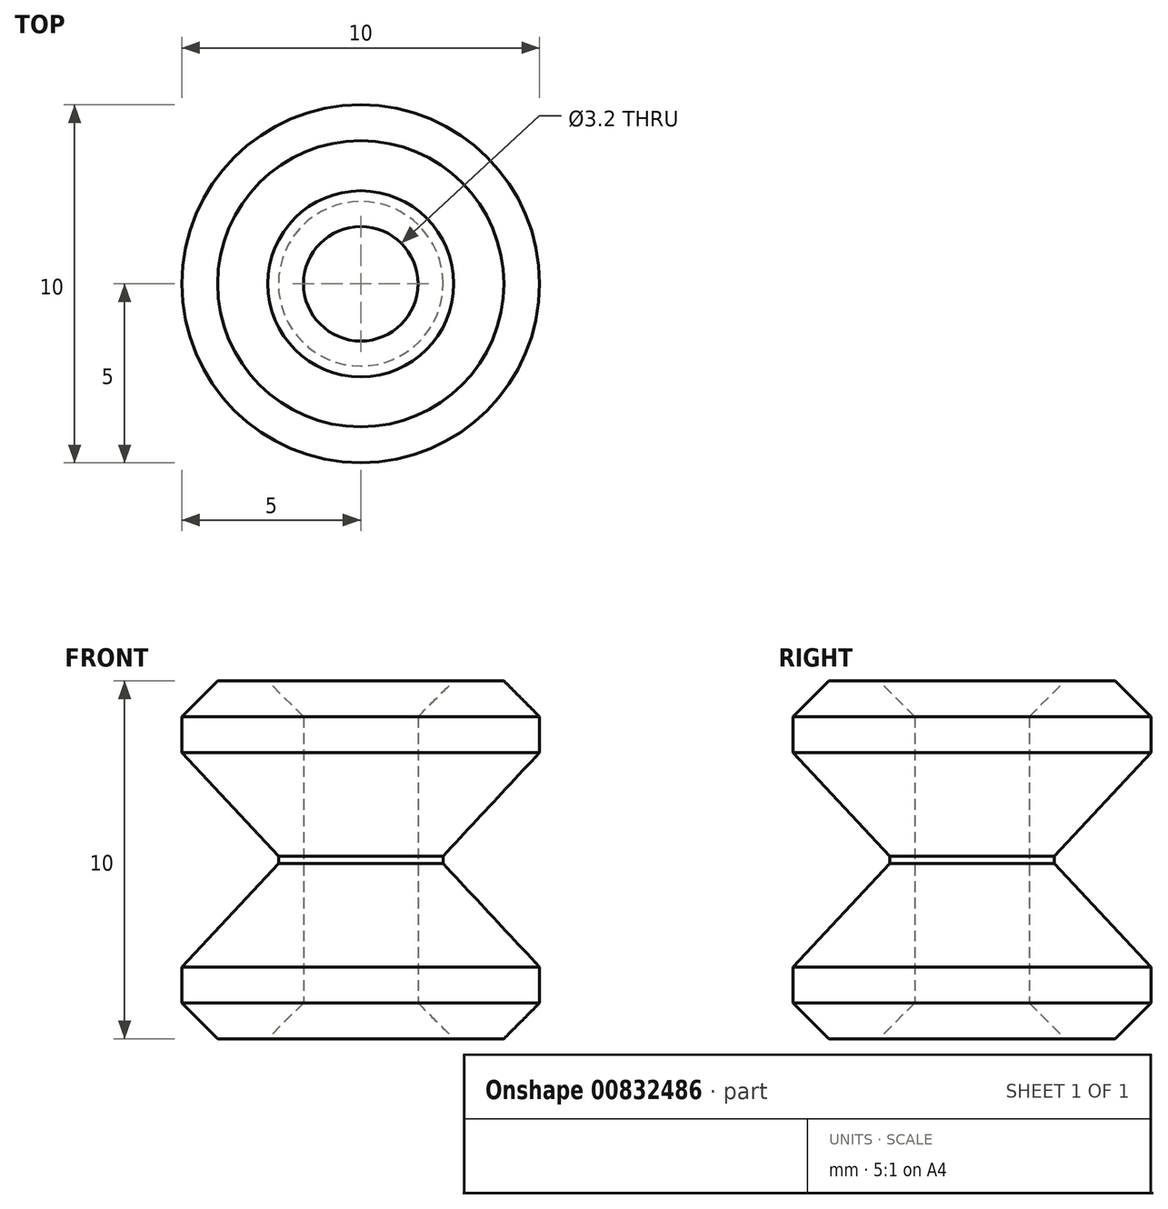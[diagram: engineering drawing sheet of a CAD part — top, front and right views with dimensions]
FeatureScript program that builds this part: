
annotation { "Feature Type Name" : "Feature", "Feature Type Description" : "" }
export const myFeature = defineFeature(function(context is Context, id is Id, definition is map)
    precondition{}
    {
        {
            var Q0;
            Q0=qCreatedBy(makeId("Top.planeOp"),FACE);
            var sketch = newSketch(context, id + "F0", { "sketchPlane" : qUnion([Q0])});
            skCircle(sketch, "E0", {"center": v(0, 0) * mm, "radius": 5 * mm});
            skCircle(sketch, "E1", {"center": v(0, 0) * mm, "radius": 1.6 * mm});
            skSolve(sketch);
        }
        {
            var Q0;
            Q0=makeQuery(id+"F0.imprint","IMPRINT",FACE,{"disambiguationData":[TD([[makeQuery(id+"F0.imprint","IMPRINT",EDGE,{"derivedFrom":sQuery(id+"F0.wireOp",EDGE,"E0")}),1.0]])]});
            extrude(context, id + "F1", {"entities" : qUnion([Q0]), "depth" : 10 * mm, "offsetDistance" : 25 * mm});
        }
        {
            var Q0;
            Q0=qCreatedBy(makeId("Front.planeOp"),FACE);
            var sketch = newSketch(context, id + "F2", { "sketchPlane" : qUnion([Q0])});
            skLineSegment(sketch, "E2", {"start": v(5, 8) * mm, "end": v(2.3, 5.1) * mm});
            skLineSegment(sketch, "E3", {"start": v(2.3, 5.1) * mm, "end": v(2.3, 4.9) * mm});
            skLineSegment(sketch, "E4", {"start": v(2.3, 4.9) * mm, "end": v(5, 2) * mm});
            skLineSegment(sketch, "E5", {"start": v(5, 6.45) * mm, "end": v(5, 4.2) * mm, "construction": true});
            skLineSegment(sketch, "E6", {"start": v(5, 8) * mm, "end": v(5, 2) * mm});
            skSolve(sketch);
        }
        {
            var Q0;
            Q0=makeQuery(id+"F2.imprint","IMPRINT",FACE,{"disambiguationData":[TD([[makeQuery(id+"F2.imprint","IMPRINT",EDGE,{"derivedFrom":sQuery(id+"F2.wireOp",EDGE,"E2")}),1.0]])]});
            var Q1;
            Q1=makeQuery(id+"F1.opExtrude","CAP_EDGE",EDGE,{"disambiguationData":[OSD([sQuery(id+"F0.wireOp",EDGE,"E0")])],"isStart":false});
            revolve(context, id + "F3", {"operationType" : NewBodyOperationType.REMOVE, "surfaceOperationType" : NewSurfaceOperationType.NEW, "entities" : qUnion([Q0]), "axis" : qUnion([Q1]), "revolveType" : RevolveType.FULL, "oppositeDirection" : true});
        }
        {
            var Q0;
            Q0=makeQuery(id+"F1.opExtrude","CAP_EDGE",EDGE,{"disambiguationData":[OSD([sQuery(id+"F0.wireOp",EDGE,"E0")])],"isStart":false});
            var Q1;
            Q1=makeQuery(id+"F1.opExtrude","CAP_EDGE",EDGE,{"disambiguationData":[OSD([sQuery(id+"F0.wireOp",EDGE,"E0")])],"isStart":true});
            var Q2;
            Q2=makeQuery(id+"F1.opExtrude","CAP_EDGE",EDGE,{"disambiguationData":[OSD([sQuery(id+"F0.wireOp",EDGE,"E1")])],"isStart":false});
            var Q3;
            Q3=makeQuery(id+"F1.opExtrude","CAP_EDGE",EDGE,{"disambiguationData":[OSD([sQuery(id+"F0.wireOp",EDGE,"E1")])],"isStart":true});
            chamfer(context, id + "F4", {"entities" : qUnion([Q0, Q1, Q2, Q3]), "width" : 1 * mm, "tangentPropagation" : true});
        }
    });
